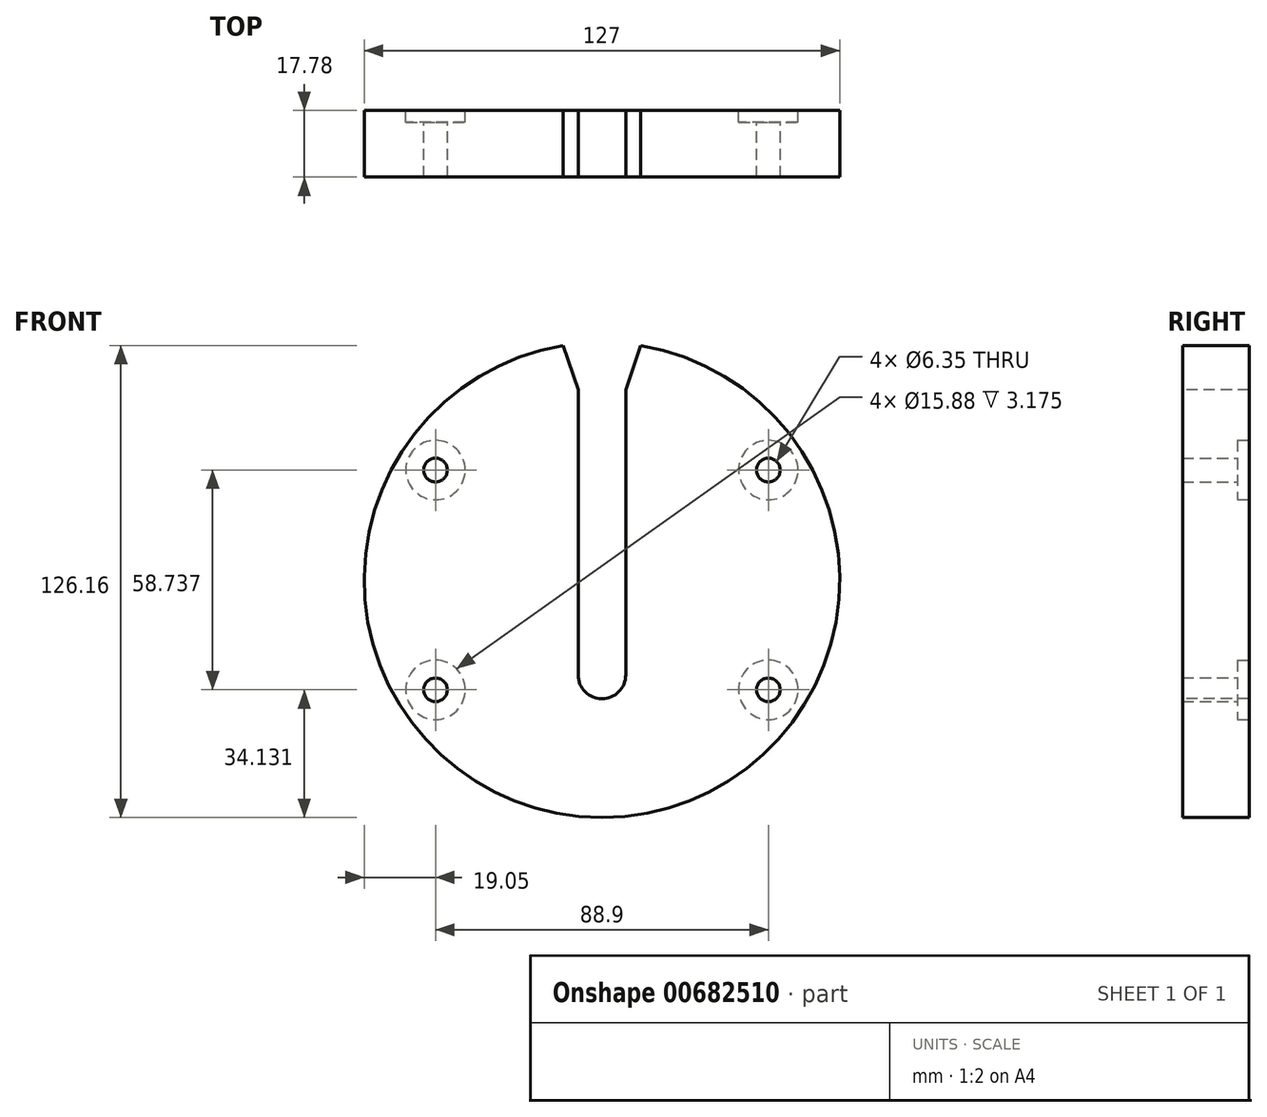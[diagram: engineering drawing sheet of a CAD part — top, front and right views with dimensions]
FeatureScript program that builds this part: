
annotation { "Feature Type Name" : "Feature", "Feature Type Description" : "" }
export const myFeature = defineFeature(function(context is Context, id is Id, definition is map)
    precondition{}
    {
        {
            var Q0;
            Q0=qCreatedBy(makeId("Front.planeOp"),FACE);
            var sketch = newSketch(context, id + "F0", { "sketchPlane" : qUnion([Q0])});
            skPoint(sketch, "E0", {"position": v(-44.45, 29.37) * mm});
            skPoint(sketch, "E1", {"position": v(44.45, 29.37) * mm});
            skPoint(sketch, "E2", {"position": v(44.45, -29.37) * mm});
            skPoint(sketch, "E3", {"position": v(-44.45, -29.37) * mm});
            skLineSegment(sketch, "E4", {"start": v(0, 0) * mm, "end": v(0, 0) * mm});
            skCircle(sketch, "E5", {"center": v(0, 0) * mm, "radius": 63.5 * mm});
            skSolve(sketch);
        }
        {
            var Q0;
            Q0=makeQuery(id+"F0.imprint","IMPRINT",FACE,{"disambiguationData":[TD([[makeQuery(id+"F0.imprint","IMPRINT",EDGE,{"derivedFrom":sQuery(id+"F0.wireOp",EDGE,"0SG29FPq-SwXB-MbIm-qeFK-cjPBrF2aFsSZ.bottom")}),1.0]])]});
            var Q1;
            Q1=makeQuery(id+"F0.imprint","IMPRINT",FACE,{"disambiguationData":[TD([[makeQuery(id+"F0.imprint","IMPRINT",EDGE,{"derivedFrom":sQuery(id+"F0.wireOp",EDGE,"0SG29FPq-SwXB-MbIm-qeFK-cjPBrF2aFsSZ.top")}),-1.0]])]});
            var Q2;
            Q2=makeQuery(id+"F0.imprint","IMPRINT",FACE,{"disambiguationData":[TD([[makeQuery(id+"F0.imprint","IMPRINT",EDGE,{"derivedFrom":sQuery(id+"F0.wireOp",EDGE,"E5")}),1.0]])]});
            extrude(context, id + "F1", {"entities" : qUnion([Q0, Q1, Q2]), "depth" : 17.78 * mm, "offsetDistance" : 25.4 * mm});
        }
        {
            var Q0;
            Q0=sQuery(id+"F0.wireOp",VERTEX,"E1");
            var Q1;
            Q1=sQuery(id+"F0.wireOp",VERTEX,"E0");
            var Q2;
            Q2=sQuery(id+"F0.wireOp",VERTEX,"E3");
            var Q3;
            Q3=sQuery(id+"F0.wireOp",VERTEX,"E2");
            var Q4;
            Q4=makeQuery(id+"F1.opExtrude","SWEPT_BODY",BODY,{"disambiguationData":[OSD([sQuery(id+"F0.wireOp",EDGE,"E5")])]});
            hole(context, id + "F2", {"style" : HoleStyle.C_BORE, "endStyle" : HoleEndStyle.THROUGH, "oppositeDirection" : true, "holeDiameter" : 6.35 * mm, "cBoreDiameter" : 15.88 * mm, "cBoreDepth" : 3.17 * mm, "majorDiameter" : 6.35 * mm, "isTappedThrough" : true, "tappedDepth" : 12.7 * mm, "tapClearance" : 3, "locations" : qUnion([Q0, Q1, Q2, Q3]), "scope" : qUnion([Q4])});
        }
        {
            var Q0;
            Q0=makeQuery(id+"F1.opExtrude","CAP_FACE",FACE,{"disambiguationData":[OSD([sQuery(id+"F0.wireOp",EDGE,"E5")])],"isStart":false});
            var sketch = newSketch(context, id + "F3", { "sketchPlane" : qUnion([Q0])});
            skPoint(sketch, "E6", {"position": v(-44.45, 29.37) * mm});
            skPoint(sketch, "E7", {"position": v(-44.45, -29.37) * mm});
            skPoint(sketch, "E8", {"position": v(44.45, -29.37) * mm});
            skPoint(sketch, "E9", {"position": v(44.45, 29.37) * mm});
            skSolve(sketch);
        }
        {
            var Q0;
            Q0=sQuery(id+"F3.wireOp",VERTEX,"E6");
            var Q1;
            Q1=sQuery(id+"F3.wireOp",VERTEX,"E9");
            var Q2;
            Q2=sQuery(id+"F3.wireOp",VERTEX,"E8");
            var Q3;
            Q3=sQuery(id+"F3.wireOp",VERTEX,"E7");
            var Q4;
            Q4=makeQuery(id+"F1.opExtrude","SWEPT_BODY",BODY,{"disambiguationData":[OSD([sQuery(id+"F0.wireOp",EDGE,"E5")])]});
            hole(context, id + "F4", {"style" : HoleStyle.SIMPLE, "endStyle" : HoleEndStyle.BLIND, "holeDiameter" : 13 / 812.8 * mm, "majorDiameter" : 6.35 * mm, "holeDepth" : 6.35 * mm, "isTappedThrough" : true, "tappedDepth" : 12.7 * mm, "tapClearance" : 3, "startFromSketch" : true, "locations" : qUnion([Q0, Q1, Q2, Q3]), "scope" : qUnion([Q4])});
        }
        {
            var Q0;
            Q0=makeQuery(id+"F1.opExtrude","CAP_FACE",FACE,{"disambiguationData":[OSD([sQuery(id+"F0.wireOp",EDGE,"E5")])],"isStart":false});
            var sketch = newSketch(context, id + "F5", { "sketchPlane" : qUnion([Q0])});
            skLineSegment(sketch, "E10", {"start": v(-6.35, 50.8) * mm, "end": v(-6.35, -25.4) * mm});
            skLineSegment(sketch, "E11", {"start": v(6.35, -25.4) * mm, "end": v(6.35, 50.8) * mm});
            skArc(sketch, "E12", {"start": v(-6.35, -25.4) * mm, "mid": v(0, -31.75) * mm, "end": v(6.35, -25.4) * mm});
            skLineSegment(sketch, "E13", {"start": v(10.31, 62.66) * mm, "end": v(6.35, 50.8) * mm});
            skLineSegment(sketch, "E14", {"start": v(-6.35, 50.8) * mm, "end": v(-10.31, 62.66) * mm});
            skPoint(sketch, "E15.orphan", {"position": v(6.35, 63.18) * mm});
            skSolve(sketch);
        }
        {
            var Q0;
            {var subQ0=sQuery(id+"F5.wireOp",EDGE,"E10");Q0=makeQuery(id+"F5.imprint","IMPRINT",FACE,{"disambiguationData":[TD([[makeQuery(id+"F5.imprint","IMPRINT",EDGE,{"derivedFrom":subQ0}),1.0]])]});}
            extrude(context, id + "F6", {"entities" : qUnion([Q0]), "operationType" : NewBodyOperationType.REMOVE, "oppositeDirection" : true, "depth" : 25.4 * mm, "offsetDistance" : 25.4 * mm});
        }
    });
